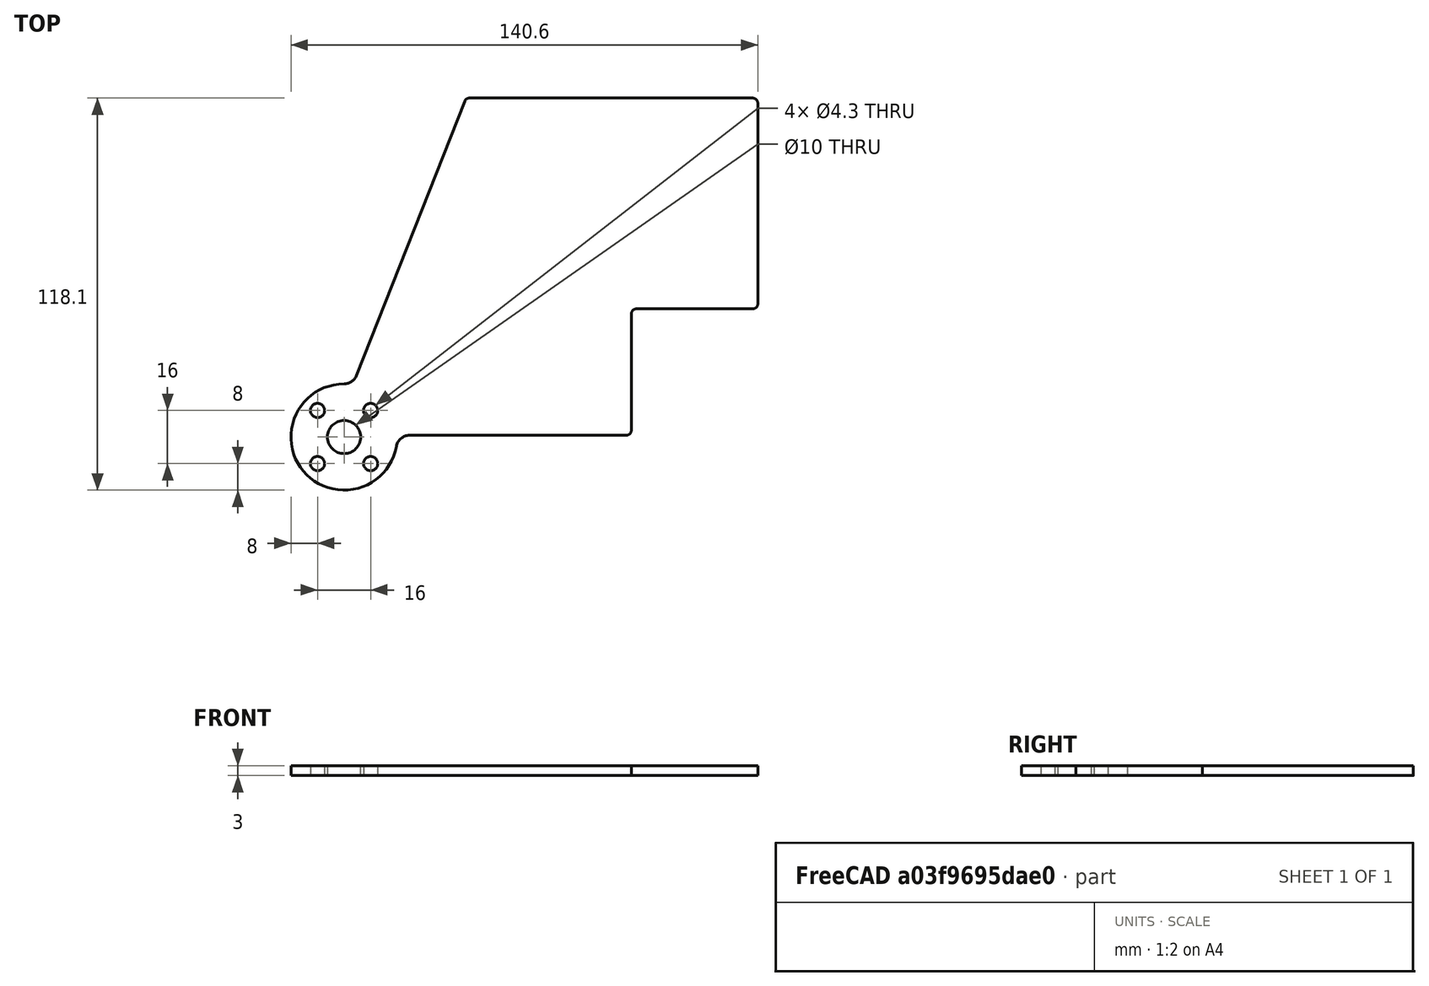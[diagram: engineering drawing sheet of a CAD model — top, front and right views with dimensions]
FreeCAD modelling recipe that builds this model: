
FCSTD DOCUMENT  (FreeCAD 0.21R33675 (Git))
Label: tmaze_door_4in_with_extension
License: All rights reserved
LicenseURL: http://en.wikipedia.org/wiki/All_rights_reserved
objects: Sketcher::SketchObject×1, Spreadsheet::Sheet×1, PartDesign::Pad×1, PartDesign::Body×1
note: 4 computed .brp shape members not serialized (recipe doc carries the construction recipe); baked Part::Feature solids carry a one-line shape summary decoded from their .brp

FEATURE [Sketcher::SketchObject] Sketch  label="DoorSketch"
  FullyConstrained = true
  MapMode = 5
  Support = -> [XY_Plane]
  expr: Constraints[11] = Spreadsheet.DoorFilletRadius
  expr: Constraints[1] = Spreadsheet.DoorHubDiameter
  expr: Constraints[29] = Spreadsheet.DoorToMazeFloorMargin
  expr: Constraints[34] = Spreadsheet.DoorHubFilletRadius
  expr: Constraints[3] = Spreadsheet.DoorLength
  expr: Constraints[40] = Spreadsheet.ServoSplineToMazeFloorDistance
  expr: Constraints[58] = Spreadsheet.ServoHubMountThruHoleDiameter
  expr: Constraints[59] = Spreadsheet.ServoHubMountHoleSpacing
  expr: Constraints[5] = Spreadsheet.DoorHeight
  expr: Constraints[61] = Spreadsheet.ServoHubCenterHoleDiameter
  expr: Constraints[64] = Spreadsheet.DoorExtensionStartHeight
  expr: Constraints[66] = Spreadsheet.DoorExtensionLength
  sketch-geometry (36):
    g0: Circle CenterX=0 CenterY=0 CenterZ=0 NormalX=0 NormalY=0 NormalZ=1 AngleXU=0 Radius=16
    g1: LineSegment StartX=36.7 StartY=0.5 StartZ=0 EndX=85 EndY=0.5 EndZ=0
    g2: LineSegment StartX=86.5 StartY=2 StartZ=0 EndX=86.5 EndY=100.6 EndZ=0
    g3: LineSegment StartX=85 StartY=102.1 StartZ=0 EndX=37.7206 EndY=102.1 EndZ=0
    g4: LineSegment StartX=3.72075 StartY=18.5317 StartZ=0 EndX=36.3253 EndY=101.151 EndZ=0
    g5: ArcOfCircle CenterX=85 CenterY=2 CenterZ=0 NormalX=0 NormalY=0 NormalZ=1 AngleXU=0 Radius=1.5 StartAngle=4.71239 EndAngle=6.28319
    g6: GeomPoint X=86.5 Y=0.5 Z=0
    g7: ArcOfCircle CenterX=85 CenterY=100.6 CenterZ=0 NormalX=0 NormalY=0 NormalZ=1 AngleXU=0 Radius=1.5 StartAngle=4.5e-15 EndAngle=1.5708
    g8: GeomPoint X=86.5 Y=102.1 Z=0
    g9: LineSegment StartX=36.7 StartY=102.1 StartZ=0 EndX=36.7 EndY=0.5 EndZ=0
    g10: ArcOfCircle CenterX=37.7206 CenterY=100.6 CenterZ=0 NormalX=0 NormalY=0 NormalZ=1 AngleXU=0 Radius=1.5 StartAngle=1.5708 EndAngle=2.76572
    g11: GeomPoint X=36.7 Y=102.1 Z=0
    g12: ArcOfCircle CenterX=0 CenterY=0 CenterZ=0 NormalX=0 NormalY=0 NormalZ=1 AngleXU=0 Radius=16 StartAngle=1.5708 EndAngle=6.10728
    g13: LineSegment StartX=36.7 StartY=0 StartZ=0 EndX=36.7 EndY=0.5 EndZ=0
    g14: LineSegment StartX=36.7 StartY=0.5 StartZ=0 EndX=19.6914 EndY=0.5 EndZ=0
    g15: ArcOfCircle CenterX=19.6914 CenterY=-3.5 CenterZ=0 NormalX=0 NormalY=0 NormalZ=1 AngleXU=0 Radius=4 StartAngle=1.5708 EndAngle=2.96569
    g16: ArcOfCircle CenterX=5e-16 CenterY=20 CenterZ=0 NormalX=0 NormalY=0 NormalZ=1 AngleXU=0 Radius=4 StartAngle=4.71239 EndAngle=5.90731
    g17: LineSegment StartX=-8 StartY=8 StartZ=0 EndX=8 EndY=8 EndZ=0
    g18: LineSegment StartX=8 StartY=8 StartZ=0 EndX=8 EndY=-8 EndZ=0
    g19: LineSegment StartX=8 StartY=-8 StartZ=0 EndX=-8 EndY=-8 EndZ=0
    g20: LineSegment StartX=-8 StartY=-8 StartZ=0 EndX=-8 EndY=8 EndZ=0
    g21: Circle CenterX=-8 CenterY=8 CenterZ=0 NormalX=0 NormalY=0 NormalZ=1 AngleXU=0 Radius=2.15
    g22: Circle CenterX=8 CenterY=8 CenterZ=0 NormalX=0 NormalY=0 NormalZ=1 AngleXU=0 Radius=2.15
    g23: Circle CenterX=-8 CenterY=-8 CenterZ=0 NormalX=0 NormalY=0 NormalZ=1 AngleXU=0 Radius=2.15
    g24: Circle CenterX=8 CenterY=-8 CenterZ=0 NormalX=0 NormalY=0 NormalZ=1 AngleXU=0 Radius=2.15
    g25: Circle CenterX=0 CenterY=0 CenterZ=0 NormalX=0 NormalY=0 NormalZ=1 AngleXU=0 Radius=5
    g26: LineSegment StartX=86.5 StartY=2 StartZ=0 EndX=86.5 EndY=37.1 EndZ=0
    g27: LineSegment StartX=88 StartY=38.6 StartZ=0 EndX=123.1 EndY=38.6 EndZ=0
    g28: LineSegment StartX=124.6 StartY=40.1 StartZ=0 EndX=124.6 EndY=100.6 EndZ=0
    g29: LineSegment StartX=123.1 StartY=102.1 StartZ=0 EndX=85 EndY=102.1 EndZ=0
    g30: ArcOfCircle CenterX=88 CenterY=37.1 CenterZ=0 NormalX=0 NormalY=0 NormalZ=1 AngleXU=0 Radius=1.5 StartAngle=1.5708 EndAngle=3.14159
    g31: GeomPoint X=86.5 Y=38.6 Z=0
    g32: ArcOfCircle CenterX=123.1 CenterY=40.1 CenterZ=0 NormalX=0 NormalY=0 NormalZ=1 AngleXU=0 Radius=1.5 StartAngle=4.71239 EndAngle=6.28319
    g33: GeomPoint X=124.6 Y=38.6 Z=0
    g34: ArcOfCircle CenterX=123.1 CenterY=100.6 CenterZ=0 NormalX=0 NormalY=0 NormalZ=1 AngleXU=0 Radius=1.5 StartAngle=0 EndAngle=1.5708
    g35: GeomPoint X=124.6 Y=102.1 Z=0
  constraints (85):
    c: Coincident(g0,g-1)
    c: Diameter(g0) = 32
    c: Horizontal(g1)
    c: DistanceX(g1,g6) = 49.8
    c: Vertical(g2)
    c: DistanceY(g6,g8) = 101.6
    c: Horizontal(g3)
    c: PointOnObject(g6,g1)
    c: PointOnObject(g6,g2)
    c: Tangent(g1,g5) = -1.5708
    c: Tangent(g2,g5) = -1.5708
    c: Radius(g5) = 1.5
    c: PointOnObject(g8,g3)
    c: PointOnObject(g8,g2)
    c: Tangent(g3,g7) = -1.5708
    c: Tangent(g2,g7) = -1.5708
    c: Equal(g5,g7)
    c: Coincident(g9,g11)
    c: Vertical(g9)
    c: PointOnObject(g11,g4)
    c: PointOnObject(g11,g3)
    c: Tangent(g4,g10) = 1.5708
    c: Tangent(g3,g10) = -1.5708
    c: Equal(g7,g10)
    c: Coincident(g12,g0)
    c: PointOnObject(g12,g0)
    c: PointOnObject(g13,g-1)
    c: Vertical(g13)
    c: Coincident(g13,g1)
    c: DistanceY(g13,g13) = 0.5
    c: Coincident(g14,g1)
    c: Horizontal(g14)
    c: Tangent(g15,g14) = -1.5708
    c: Tangent(g15,g12) = 1.5708
    c: Radius(g15) = 4
    c: Tangent(g12,g16) = 1.5708
    c: Tangent(g4,g16) = -1.5708
    c: Equal(g16,g15)
    c: PointOnObject(g12,g-2)
    c: Coincident(g9,g1)
    c: DistanceX(g12,g1) = 36.7
    c: Coincident(g17,g18)
    c: Coincident(g18,g19)
    c: Coincident(g19,g20)
    c: Coincident(g20,g17)
    c: Horizontal(g17)
    c: Horizontal(g19)
    c: Vertical(g18)
    c: Vertical(g20)
    c: Symmetric(g17,g18,g12)
    c: Equal(g20,g17)
    c: Coincident(g21,g17)
    c: Coincident(g22,g17)
    c: Coincident(g23,g19)
    c: Coincident(g24,g18)
    c: Equal(g21,g22)
    c: Equal(g22,g24)
    c: Equal(g24,g23)
    c: Diameter(g21) = 4.3
    c: DistanceX(g17,g17) = 16
    c: Coincident(g25,g12)
    c: Diameter(g25) = 10
    c: Coincident(g26,g5)
    c: Vertical(g26)
    c: DistanceY(g1,g31) = 38.1
    c: Horizontal(g27)
    c: DistanceX(g31,g33) = 38.1
    c: Vertical(g28)
    c: Horizontal(g29)
    c: Coincident(g3,g29)
    c: PointOnObject(g31,g26)
    c: PointOnObject(g31,g27)
    c: Tangent(g26,g30) = 1.5708
    c: Tangent(g27,g30) = 1.5708
    c: PointOnObject(g33,g27)
    c: PointOnObject(g33,g28)
    c: Tangent(g27,g32) = -1.5708
    c: Tangent(g28,g32) = -1.5708
    c: PointOnObject(g35,g29)
    c: PointOnObject(g35,g28)
    c: Tangent(g29,g34) = -1.5708
    c: Tangent(g28,g34) = -1.5708
    c: Equal(g5,g30)
    c: Equal(g30,g32)
    c: Equal(g5,g34)
FEATURE [Spreadsheet::Sheet] Spreadsheet
  cells = A2='Servo Hub Parameters; A3='ServoHubDiameter; B3(ServoHubDiameter)==32 mm; A4='ServoHubMountHoleSpacing; B4(ServoHubMountHoleSpacing)==16 mm; A5='ServoHubMountThruHoleDiameter; B5(ServoHubMountThruHoleDiameter)==4.3 mm; A6='ServoHubCenterHoleDiameter; B6(ServoHubCenterHoleDiameter)==10 mm; A7='ServoSplineToServoMountHoleDistance; B7(ServoSplineToServoMountHoleDistance)==14.2 mm; A8='ServoMountHoleToBracketBndryDistance; B8(ServoMountHoleToBracketBndryDistance)==3.5 mm; A9='ServoMarginToMountPlate; B9(ServoMarginToMountPlate)==10 mm; A10='MountPlateThickness; B10(MountPlateThickness)==9 mm; A11='MazeWidth; B11(MazeWidth)==2 in; A14='Design Parameters; A15='DoorHubDiameter; B15(DoorHubDiameter)==ServoHubDiameter; A16='DoorToMazeFloorMargin; B16(DoorToMazeFloorMargin)==0.5 mm; A17='DoorToMazeWallMargin; B17(DoorToMazeWallMargin)==1 mm; A18='ServoSplineToMazeFloorDistance; B18(ServoSplineToMazeFloorDistance)==ServoSplineToServoMountHoleDistance + ServoMountHoleToBracketBndryDistance + ServoMarginToMountPlate + MountPlateThickness; A19='DoorLength; B19(DoorLength)==MazeWidth - DoorToMazeWallMargin; A20='DoorHeight; B20(DoorHeight)==4 in; A21='DoorFilletRadius; B21(DoorFilletRadius)==1.5 mm; A22='DoorHubFilletRadius; B22(DoorHubFilletRadius)==4 mm; A23='DoorThickness; B23(DoorThickness)==3 mm; A25='DoorExtensionStartHeight; B25(DoorExtensionStartHeight)==1.5 in; A26='DoorExtensionLength; B26(DoorExtensionLength)==1.5 in
FEATURE [PartDesign::Pad] Pad
  Direction = (0,0,1)
  Length = 3
  Length2 = 10
  Profile = -> Sketch
  ReferenceAxis = -> Sketch [N_Axis]
  Type = 0
  expr: Length = Spreadsheet.DoorThickness
FEATURE [PartDesign::Body] Body
  Group = -> [Sketch,Pad]
  Origin = -> Origin
  Tip = -> Pad
